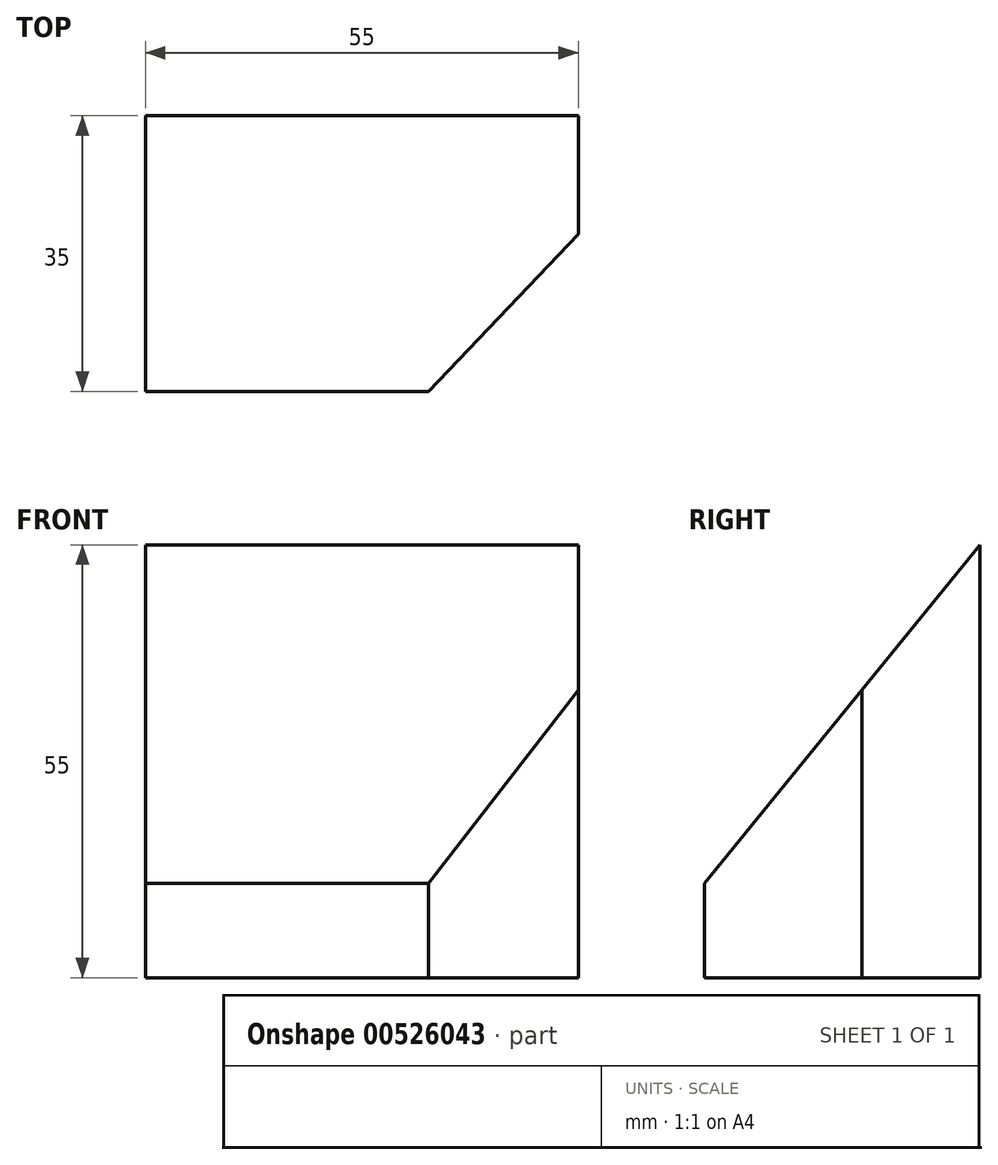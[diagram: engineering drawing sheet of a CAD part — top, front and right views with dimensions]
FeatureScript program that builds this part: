
annotation { "Feature Type Name" : "Feature", "Feature Type Description" : "" }
export const myFeature = defineFeature(function(context is Context, id is Id, definition is map)
    precondition{}
    {
        {
            var Q0;
            Q0=qCreatedBy(makeId("Front.planeOp"),FACE);
            var sketch = newSketch(context, id + "F0", { "sketchPlane" : qUnion([Q0])});
            skLineSegment(sketch, "E0.bottom", {"start": v(27.5, 27.5) * mm, "end": v(-27.5, 27.5) * mm});
            skLineSegment(sketch, "E0.top", {"start": v(27.5, -27.5) * mm, "end": v(-27.5, -27.5) * mm});
            skLineSegment(sketch, "E0.left", {"start": v(27.5, 27.5) * mm, "end": v(27.5, -27.5) * mm});
            skLineSegment(sketch, "E0.right", {"start": v(-27.5, 27.5) * mm, "end": v(-27.5, -27.5) * mm});
            skPoint(sketch, "E0.middle", {"position": v(0, 0) * mm});
            skSolve(sketch);
        }
        {
            var Q0;
            Q0=makeQuery(id+"F0.imprint","IMPRINT",FACE,{"disambiguationData":[TD([[makeQuery(id+"F0.imprint","IMPRINT",EDGE,{"derivedFrom":sQuery(id+"F0.wireOp",EDGE,"E0.bottom")}),1.0]])]});
            extrude(context, id + "F1", {"entities" : qUnion([Q0]), "endBound" : BoundingType.SYMMETRIC, "depth" : 35 * mm, "offsetDistance" : 25 * mm});
        }
        {
            var Q0;
            Q0=makeQuery(id+"F1.opExtrude","SWEPT_FACE",FACE,{"disambiguationData":[OSD([sQuery(id+"F0.wireOp",EDGE,"E0.left")])]});
            var sketch = newSketch(context, id + "F2", { "sketchPlane" : qUnion([Q0])});
            skLineSegment(sketch, "E1", {"start": v(-17.5, -15.5) * mm, "end": v(17.5, 27.5) * mm});
            skLineSegment(sketch, "E2", {"start": v(17.5, 27.5) * mm, "end": v(-17.5, 27.5) * mm});
            skLineSegment(sketch, "E3", {"start": v(-17.5, 27.5) * mm, "end": v(-17.5, -15.5) * mm});
            skSolve(sketch);
        }
        {
            var Q0;
            Q0=makeQuery(id+"F2.imprint","IMPRINT",FACE,{"disambiguationData":[TD([[makeQuery(id+"F2.imprint","IMPRINT",EDGE,{"derivedFrom":sQuery(id+"F2.wireOp",EDGE,"E1")}),1.0]])]});
            extrude(context, id + "F3", {"entities" : qUnion([Q0]), "operationType" : NewBodyOperationType.REMOVE, "endBound" : BoundingType.THROUGH_ALL, "oppositeDirection" : true, "depth" : 25 * mm, "offsetDistance" : 25 * mm});
        }
        {
            var Q0;
            Q0=makeQuery(id+"F1.opExtrude","SWEPT_FACE",FACE,{"disambiguationData":[OSD([sQuery(id+"F0.wireOp",EDGE,"E0.top")])]});
            var sketch = newSketch(context, id + "F4", { "sketchPlane" : qUnion([Q0])});
            skLineSegment(sketch, "E4", {"start": v(27.5, -2.5) * mm, "end": v(8.5, 17.5) * mm});
            skLineSegment(sketch, "E5", {"start": v(8.5, 17.5) * mm, "end": v(27.5, 17.5) * mm});
            skLineSegment(sketch, "E6", {"start": v(27.5, 17.5) * mm, "end": v(27.5, -2.5) * mm});
            skSolve(sketch);
        }
        {
            var Q0;
            Q0=makeQuery(id+"F4.imprint","IMPRINT",FACE,{"disambiguationData":[TD([[makeQuery(id+"F4.imprint","IMPRINT",EDGE,{"derivedFrom":sQuery(id+"F4.wireOp",EDGE,"E4")}),-1.0]])]});
            extrude(context, id + "F5", {"entities" : qUnion([Q0]), "operationType" : NewBodyOperationType.REMOVE, "endBound" : BoundingType.THROUGH_ALL, "oppositeDirection" : true, "depth" : 25 * mm, "offsetDistance" : 25 * mm});
        }
    });
